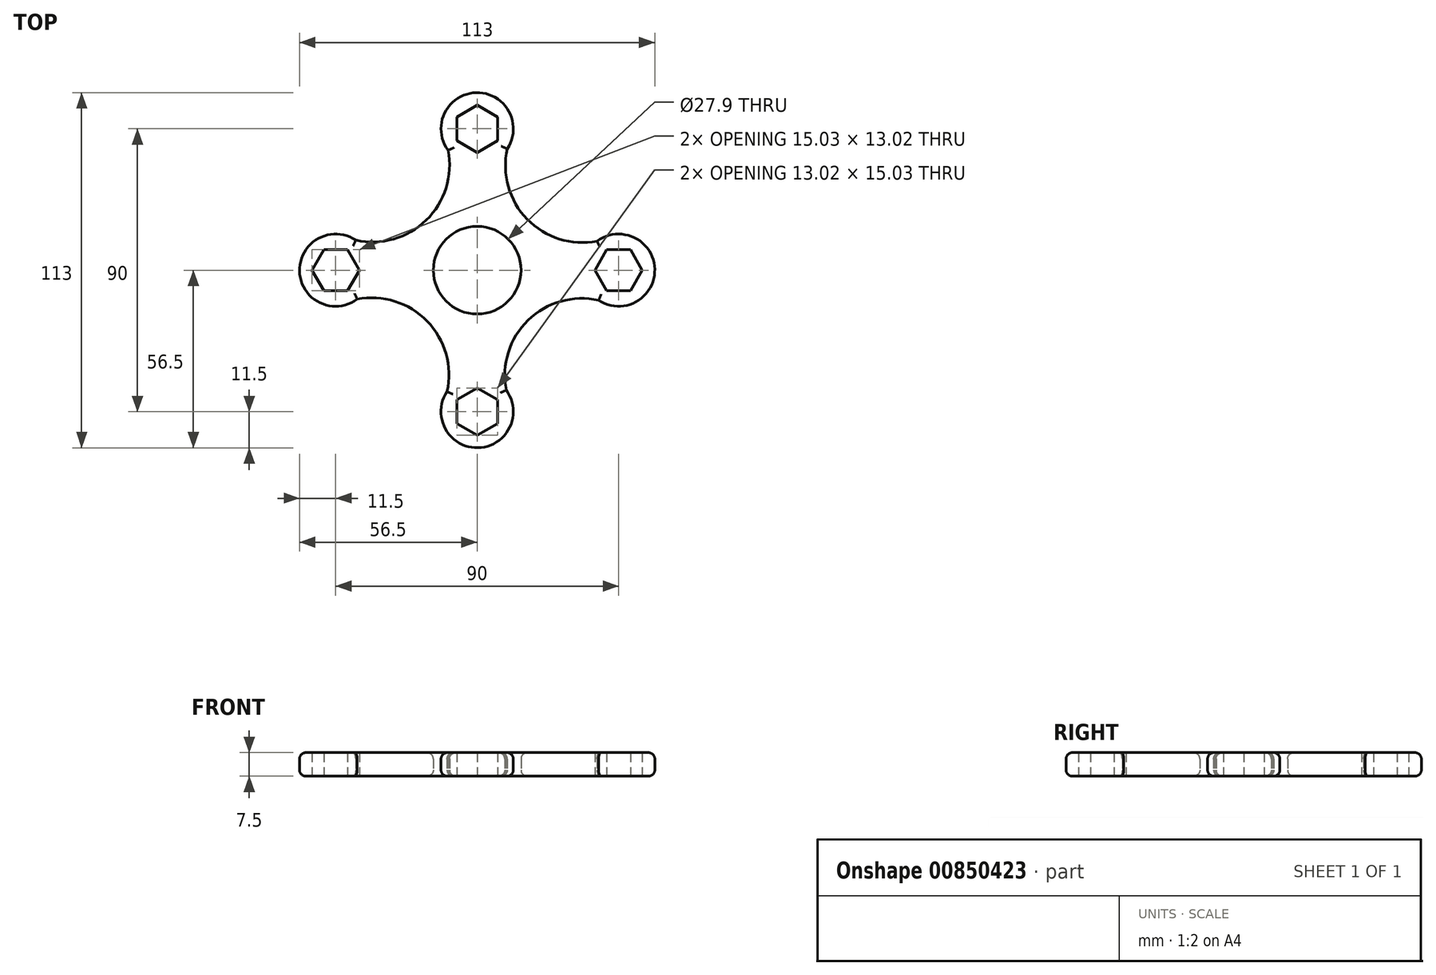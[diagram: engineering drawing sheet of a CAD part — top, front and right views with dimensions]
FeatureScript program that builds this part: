
annotation { "Feature Type Name" : "Feature", "Feature Type Description" : "" }
export const myFeature = defineFeature(function(context is Context, id is Id, definition is map)
    precondition{}
    {
        {
            var Q0;
            Q0=qCreatedBy(makeId("Top.planeOp"),FACE);
            var sketch = newSketch(context, id + "F0", { "sketchPlane" : qUnion([Q0])});
            skCircle(sketch, "E0", {"center": v(0, 0) * mm, "radius": 13.95 * mm});
            skCircle(sketch, "E1.cCircle", {"center": v(0, 45) * mm, "radius": 6.51 * mm, "construction": true});
            skLineSegment(sketch, "E1.0", {"start": v(6.51, 48.76) * mm, "end": v(6.51, 41.24) * mm});
            skLineSegment(sketch, "E1.1", {"start": v(6.51, 41.24) * mm, "end": v(0, 37.48) * mm});
            skLineSegment(sketch, "E1.2", {"start": v(0, 37.48) * mm, "end": v(-6.51, 41.24) * mm});
            skLineSegment(sketch, "E1.3", {"start": v(-6.51, 41.24) * mm, "end": v(-6.51, 48.76) * mm});
            skLineSegment(sketch, "E1.4", {"start": v(-6.51, 48.76) * mm, "end": v(0, 52.52) * mm});
            skLineSegment(sketch, "E1.5", {"start": v(0, 52.52) * mm, "end": v(6.51, 48.76) * mm});
            skPoint(sketch, "E1.0.midPoint", {"position": v(6.51, 45) * mm});
            skArc(sketch, "E2", {"start": v(9.57, 38.63) * mm, "mid": v(-0.29, 56.5) * mm, "end": v(-9.24, 38.16) * mm});
            skArc(sketch, "E3.1.0", {"start": v(-38.63, 9.57) * mm, "mid": v(-56.5, -0.29) * mm, "end": v(-38.16, -9.24) * mm});
            skLineSegment(sketch, "E3.1.1", {"start": v(-52.52, 0) * mm, "end": v(-48.76, 6.51) * mm});
            skLineSegment(sketch, "E3.1.2", {"start": v(-48.76, 6.51) * mm, "end": v(-41.24, 6.51) * mm});
            skLineSegment(sketch, "E3.1.3", {"start": v(-41.24, 6.51) * mm, "end": v(-37.48, 0) * mm});
            skCircle(sketch, "E3.1.4", {"center": v(-45, 0) * mm, "radius": 6.51 * mm, "construction": true});
            skLineSegment(sketch, "E3.1.5", {"start": v(-37.48, 0) * mm, "end": v(-41.24, -6.51) * mm});
            skLineSegment(sketch, "E3.1.6", {"start": v(-41.24, -6.51) * mm, "end": v(-48.76, -6.51) * mm});
            skLineSegment(sketch, "E3.1.7", {"start": v(-48.76, -6.51) * mm, "end": v(-52.52, 0) * mm});
            skArc(sketch, "E3.2.0", {"start": v(-9.57, -38.63) * mm, "mid": v(0.29, -56.5) * mm, "end": v(9.24, -38.16) * mm});
            skLineSegment(sketch, "E3.2.1", {"start": v(0, -52.52) * mm, "end": v(-6.51, -48.76) * mm});
            skLineSegment(sketch, "E3.2.2", {"start": v(-6.51, -48.76) * mm, "end": v(-6.51, -41.24) * mm});
            skLineSegment(sketch, "E3.2.3", {"start": v(-6.51, -41.24) * mm, "end": v(0, -37.48) * mm});
            skCircle(sketch, "E3.2.4", {"center": v(0, -45) * mm, "radius": 6.51 * mm, "construction": true});
            skLineSegment(sketch, "E3.2.5", {"start": v(0, -37.48) * mm, "end": v(6.51, -41.24) * mm});
            skLineSegment(sketch, "E3.2.6", {"start": v(6.51, -41.24) * mm, "end": v(6.51, -48.76) * mm});
            skLineSegment(sketch, "E3.2.7", {"start": v(6.5, -48.76) * mm, "end": v(0, -52.52) * mm});
            skArc(sketch, "E4.1.3.0", {"start": v(38.63, -9.57) * mm, "mid": v(56.5, 0.29) * mm, "end": v(38.16, 9.24) * mm});
            skLineSegment(sketch, "E4.2.3.0", {"start": v(52.52, 0) * mm, "end": v(48.76, -6.51) * mm});
            skLineSegment(sketch, "E4.5.3.0", {"start": v(48.76, -6.51) * mm, "end": v(41.24, -6.51) * mm});
            skLineSegment(sketch, "E4.8.3.0", {"start": v(41.24, -6.51) * mm, "end": v(37.48, 0) * mm});
            skCircle(sketch, "E4.11.3.0", {"center": v(45, 0) * mm, "radius": 6.51 * mm, "construction": true});
            skLineSegment(sketch, "E4.13.3.0", {"start": v(37.48, 0) * mm, "end": v(41.24, 6.51) * mm});
            skLineSegment(sketch, "E4.16.3.0", {"start": v(41.24, 6.51) * mm, "end": v(48.76, 6.51) * mm});
            skLineSegment(sketch, "E4.19.3.0", {"start": v(48.76, 6.5) * mm, "end": v(52.52, 0) * mm});
            skArc(sketch, "E5", {"start": v(-38.63, 9.57) * mm, "mid": v(-16.2, 15.92) * mm, "end": v(-9.24, 38.16) * mm});
            skArc(sketch, "E6.1.0", {"start": v(-9.57, -38.63) * mm, "mid": v(-15.92, -16.2) * mm, "end": v(-38.16, -9.24) * mm});
            skArc(sketch, "E6.2.0", {"start": v(38.63, -9.57) * mm, "mid": v(16.2, -15.92) * mm, "end": v(9.24, -38.16) * mm});
            skArc(sketch, "E6.3.0", {"start": v(9.57, 38.63) * mm, "mid": v(15.92, 16.2) * mm, "end": v(38.16, 9.24) * mm});
            skSolve(sketch);
        }
        {
            var Q0;
            Q0=makeQuery(id+"F0.imprint","IMPRINT",FACE,{"disambiguationData":[TD([[makeQuery(id+"F0.imprint","IMPRINT",EDGE,{"derivedFrom":sQuery(id+"F0.wireOp",EDGE,"E0")}),-1.0]])]});
            extrude(context, id + "F1", {"entities" : qUnion([Q0]), "endBound" : BoundingType.SYMMETRIC, "depth" : 7.5 * mm, "offsetDistance" : 25 * mm});
        }
        {
            var Q0;
            Q0=makeQuery(id+"F1.opExtrude","CAP_EDGE",EDGE,{"disambiguationData":[OSD([sQuery(id+"F0.wireOp",EDGE,"E3.1.0")])],"isStart":false});
            var Q1;
            Q1=makeQuery(id+"F1.opExtrude","CAP_EDGE",EDGE,{"disambiguationData":[OSD([sQuery(id+"F0.wireOp",EDGE,"E5")])],"isStart":false});
            var Q2;
            Q2=makeQuery(id+"F1.opExtrude","CAP_EDGE",EDGE,{"disambiguationData":[OSD([sQuery(id+"F0.wireOp",EDGE,"E2")])],"isStart":false});
            var Q3;
            Q3=makeQuery(id+"F1.opExtrude","CAP_EDGE",EDGE,{"disambiguationData":[OSD([sQuery(id+"F0.wireOp",EDGE,"E6.3.0")])],"isStart":false});
            var Q4;
            Q4=makeQuery(id+"F1.opExtrude","CAP_EDGE",EDGE,{"disambiguationData":[OSD([sQuery(id+"F0.wireOp",EDGE,"E4.1.3.0")])],"isStart":false});
            var Q5;
            Q5=makeQuery(id+"F1.opExtrude","CAP_EDGE",EDGE,{"disambiguationData":[OSD([sQuery(id+"F0.wireOp",EDGE,"E6.2.0")])],"isStart":false});
            var Q6;
            Q6=makeQuery(id+"F1.opExtrude","CAP_EDGE",EDGE,{"disambiguationData":[OSD([sQuery(id+"F0.wireOp",EDGE,"E3.2.0")])],"isStart":false});
            var Q7;
            Q7=makeQuery(id+"F1.opExtrude","CAP_EDGE",EDGE,{"disambiguationData":[OSD([sQuery(id+"F0.wireOp",EDGE,"E6.1.0")])],"isStart":false});
            var Q8;
            Q8=makeQuery(id+"F1.opExtrude","CAP_EDGE",EDGE,{"disambiguationData":[OSD([sQuery(id+"F0.wireOp",EDGE,"E0")])],"isStart":false});
            var Q9;
            Q9=makeQuery(id+"F1.opExtrude","CAP_EDGE",EDGE,{"disambiguationData":[OSD([sQuery(id+"F0.wireOp",EDGE,"E6.3.0")])],"isStart":true});
            var Q10;
            Q10=makeQuery(id+"F1.opExtrude","CAP_EDGE",EDGE,{"disambiguationData":[OSD([sQuery(id+"F0.wireOp",EDGE,"E2")])],"isStart":true});
            var Q11;
            Q11=makeQuery(id+"F1.opExtrude","CAP_EDGE",EDGE,{"disambiguationData":[OSD([sQuery(id+"F0.wireOp",EDGE,"E5")])],"isStart":true});
            var Q12;
            Q12=makeQuery(id+"F1.opExtrude","CAP_EDGE",EDGE,{"disambiguationData":[OSD([sQuery(id+"F0.wireOp",EDGE,"E3.1.0")])],"isStart":true});
            var Q13;
            Q13=makeQuery(id+"F1.opExtrude","CAP_EDGE",EDGE,{"disambiguationData":[OSD([sQuery(id+"F0.wireOp",EDGE,"E6.1.0")])],"isStart":true});
            var Q14;
            Q14=makeQuery(id+"F1.opExtrude","CAP_EDGE",EDGE,{"disambiguationData":[OSD([sQuery(id+"F0.wireOp",EDGE,"E3.2.0")])],"isStart":true});
            var Q15;
            Q15=makeQuery(id+"F1.opExtrude","CAP_EDGE",EDGE,{"disambiguationData":[OSD([sQuery(id+"F0.wireOp",EDGE,"E6.2.0")])],"isStart":true});
            var Q16;
            Q16=makeQuery(id+"F1.opExtrude","CAP_EDGE",EDGE,{"disambiguationData":[OSD([sQuery(id+"F0.wireOp",EDGE,"E4.1.3.0")])],"isStart":true});
            var Q17;
            Q17=makeQuery(id+"F1.opExtrude","CAP_EDGE",EDGE,{"disambiguationData":[OSD([sQuery(id+"F0.wireOp",EDGE,"E0")])],"isStart":true});
            fillet(context, id + "F2", {"entities" : qUnion([Q0, Q1, Q2, Q3, Q4, Q5, Q6, Q7, Q8, Q9, Q10, Q11, Q12, Q13, Q14, Q15, Q16, Q17]), "radius" : 2 * mm, "tangentPropagation" : true, "allowEdgeOverflow" : false});
        }
    });
